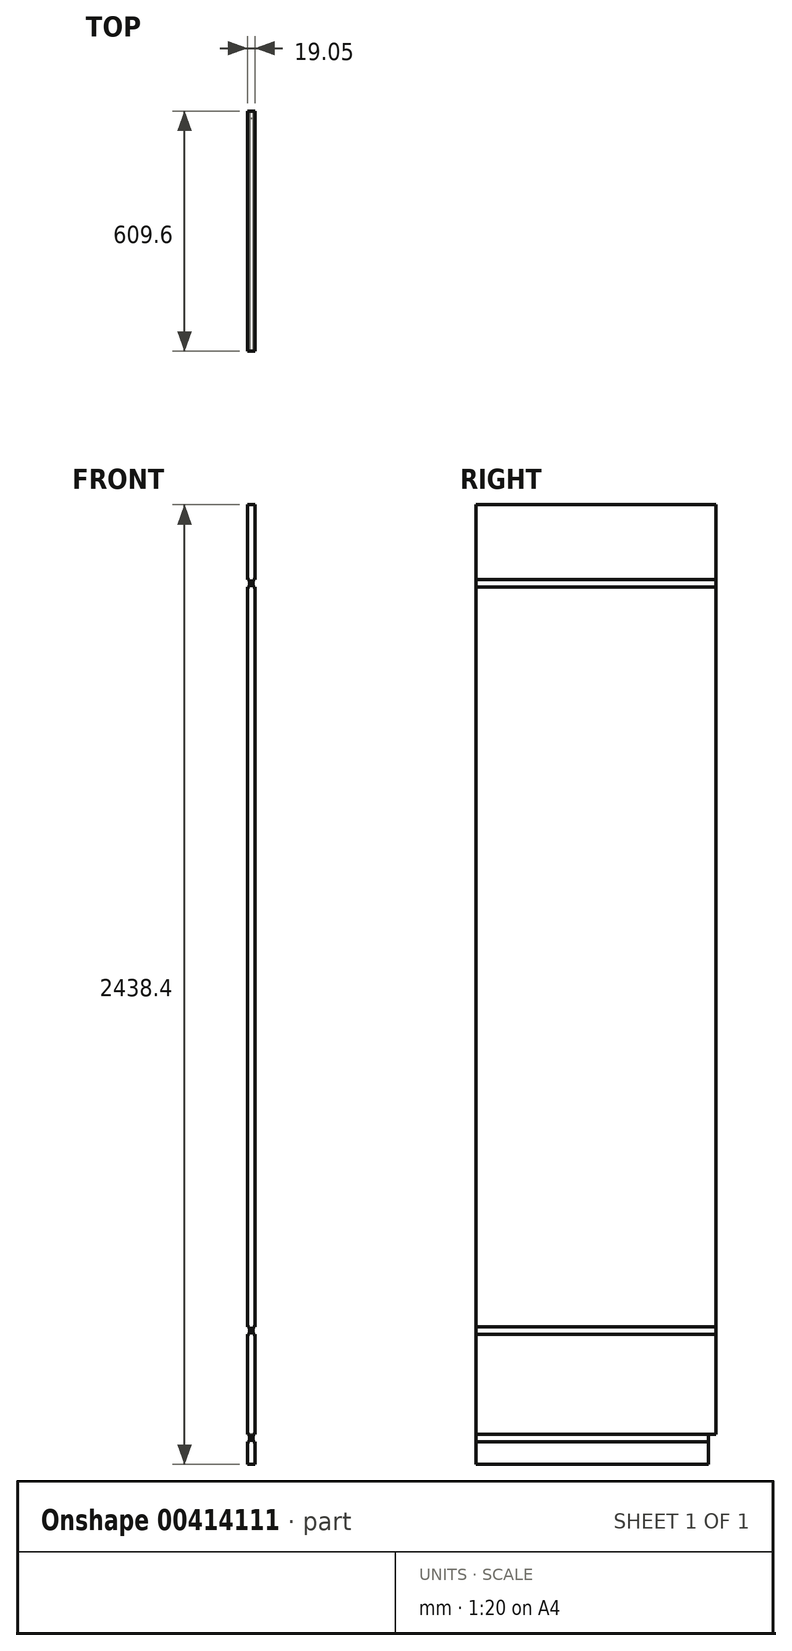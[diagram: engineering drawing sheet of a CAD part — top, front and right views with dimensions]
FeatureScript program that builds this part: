
annotation { "Feature Type Name" : "Feature", "Feature Type Description" : "" }
export const myFeature = defineFeature(function(context is Context, id is Id, definition is map)
    precondition{}
    {
        {
            var Q0;
            Q0=qCreatedBy(makeId("Front.planeOp"),FACE);
            var sketch = newSketch(context, id + "F0", { "sketchPlane" : qUnion([Q0])});
            skLineSegment(sketch, "E0", {"start": v(0, 0) * mm, "end": v(0, 2438.4) * mm});
            skLineSegment(sketch, "E1", {"start": v(0, 2438.4) * mm, "end": v(19.05, 2438.4) * mm});
            skLineSegment(sketch, "E2", {"start": v(19.05, 2438.4) * mm, "end": v(19.05, 0) * mm});
            skLineSegment(sketch, "E3", {"start": v(19.05, 0) * mm, "end": v(0, 0) * mm});
            skSolve(sketch);
        }
        {
            var Q0;
            Q0=makeQuery(id+"F0.imprint","IMPRINT",FACE,{"disambiguationData":[TD([[makeQuery(id+"F0.imprint","IMPRINT",EDGE,{"derivedFrom":sQuery(id+"F0.wireOp",EDGE,"E0")}),-1.0]])]});
            extrude(context, id + "F1", {"entities" : qUnion([Q0]), "depth" : 609.6 * mm});
        }
        {
            var Q0;
            Q0=makeQuery(id+"F1.opExtrude","SWEPT_FACE",FACE,{"disambiguationData":[OSD([sQuery(id+"F0.wireOp",EDGE,"E0")])]});
            var sketch = newSketch(context, id + "F2", { "sketchPlane" : qUnion([Q0])});
            skLineSegment(sketch, "E4.bottom", {"start": v(0, 0) * mm, "end": v(19.05, 0) * mm});
            skLineSegment(sketch, "E4.top", {"start": v(0, 76.2) * mm, "end": v(19.05, 76.2) * mm});
            skLineSegment(sketch, "E4.left", {"start": v(0, 0) * mm, "end": v(0, 76.2) * mm});
            skLineSegment(sketch, "E4.right", {"start": v(19.05, 0) * mm, "end": v(19.05, 76.2) * mm});
            skSolve(sketch);
        }
        {
            var Q0;
            Q0 = qSketchRegion(id + "F2", true);
            extrude(context, id + "F3", {"entities" : qUnion([Q0]), "operationType" : NewBodyOperationType.REMOVE, "endBound" : BoundingType.THROUGH_ALL, "oppositeDirection" : true, "depth" : 25.4 * mm});
        }
        {
            var Q0;
            Q0=makeQuery(id+"F1.opExtrude","CAP_FACE",FACE,{"disambiguationData":[OSD([sQuery(id+"F0.wireOp",EDGE,"E0"),sQuery(id+"F0.wireOp",EDGE,"E1"),sQuery(id+"F0.wireOp",EDGE,"E2"),sQuery(id+"F0.wireOp",EDGE,"E3")])],"isStart":false});
            var sketch = newSketch(context, id + "F4", { "sketchPlane" : qUnion([Q0])});
            skLineSegment(sketch, "E5.top", {"start": v(0, 57.15) * mm, "end": v(4.76, 57.15) * mm});
            skLineSegment(sketch, "E5.left", {"start": v(0, 76.2) * mm, "end": v(0, 57.15) * mm});
            skLineSegment(sketch, "E5.right", {"start": v(4.76, 76.2) * mm, "end": v(4.76, 57.15) * mm});
            skLineSegment(sketch, "E6.bottom", {"start": v(19.05, 76.2) * mm, "end": v(14.29, 76.2) * mm});
            skLineSegment(sketch, "E6.top", {"start": v(19.05, 57.15) * mm, "end": v(14.29, 57.15) * mm});
            skLineSegment(sketch, "E6.left", {"start": v(19.05, 76.2) * mm, "end": v(19.05, 57.15) * mm});
            skLineSegment(sketch, "E6.right", {"start": v(14.29, 76.2) * mm, "end": v(14.29, 57.15) * mm});
            skLineSegment(sketch, "E7.bottom", {"start": v(0, 2247.9) * mm, "end": v(4.76, 2247.9) * mm});
            skLineSegment(sketch, "E7.top", {"start": v(0, 2228.85) * mm, "end": v(4.76, 2228.85) * mm});
            skLineSegment(sketch, "E7.left", {"start": v(0, 2247.9) * mm, "end": v(0, 2228.85) * mm});
            skLineSegment(sketch, "E7.right", {"start": v(4.76, 2247.9) * mm, "end": v(4.76, 2228.85) * mm});
            skLineSegment(sketch, "E8.bottom", {"start": v(19.05, 2247.9) * mm, "end": v(14.29, 2247.9) * mm});
            skLineSegment(sketch, "E8.top", {"start": v(19.05, 2228.85) * mm, "end": v(14.29, 2228.85) * mm});
            skLineSegment(sketch, "E8.left", {"start": v(19.05, 2247.9) * mm, "end": v(19.05, 2228.85) * mm});
            skLineSegment(sketch, "E8.right", {"start": v(14.29, 2247.9) * mm, "end": v(14.29, 2228.85) * mm});
            skLineSegment(sketch, "E9", {"start": v(4.76, 76.2) * mm, "end": v(0, 76.2) * mm});
            skLineSegment(sketch, "E10.bottom", {"start": v(19.05, 349.25) * mm, "end": v(14.29, 349.25) * mm});
            skLineSegment(sketch, "E10.top", {"start": v(19.05, 330.2) * mm, "end": v(14.29, 330.2) * mm});
            skLineSegment(sketch, "E10.left", {"start": v(19.05, 349.25) * mm, "end": v(19.05, 330.2) * mm});
            skLineSegment(sketch, "E10.right", {"start": v(14.29, 349.25) * mm, "end": v(14.29, 330.2) * mm});
            skLineSegment(sketch, "E11.bottom", {"start": v(0, 349.25) * mm, "end": v(4.76, 349.25) * mm});
            skLineSegment(sketch, "E11.top", {"start": v(0, 330.2) * mm, "end": v(4.76, 330.2) * mm});
            skLineSegment(sketch, "E11.left", {"start": v(0, 349.25) * mm, "end": v(0, 330.2) * mm});
            skLineSegment(sketch, "E11.right", {"start": v(4.76, 349.25) * mm, "end": v(4.76, 330.2) * mm});
            skSolve(sketch);
        }
        {
            var Q0;
            Q0 = qSketchRegion(id + "F4", true);
            extrude(context, id + "F5", {"entities" : qUnion([Q0]), "operationType" : NewBodyOperationType.REMOVE, "endBound" : BoundingType.THROUGH_ALL, "oppositeDirection" : true, "depth" : 25.4 * mm});
        }
    });
